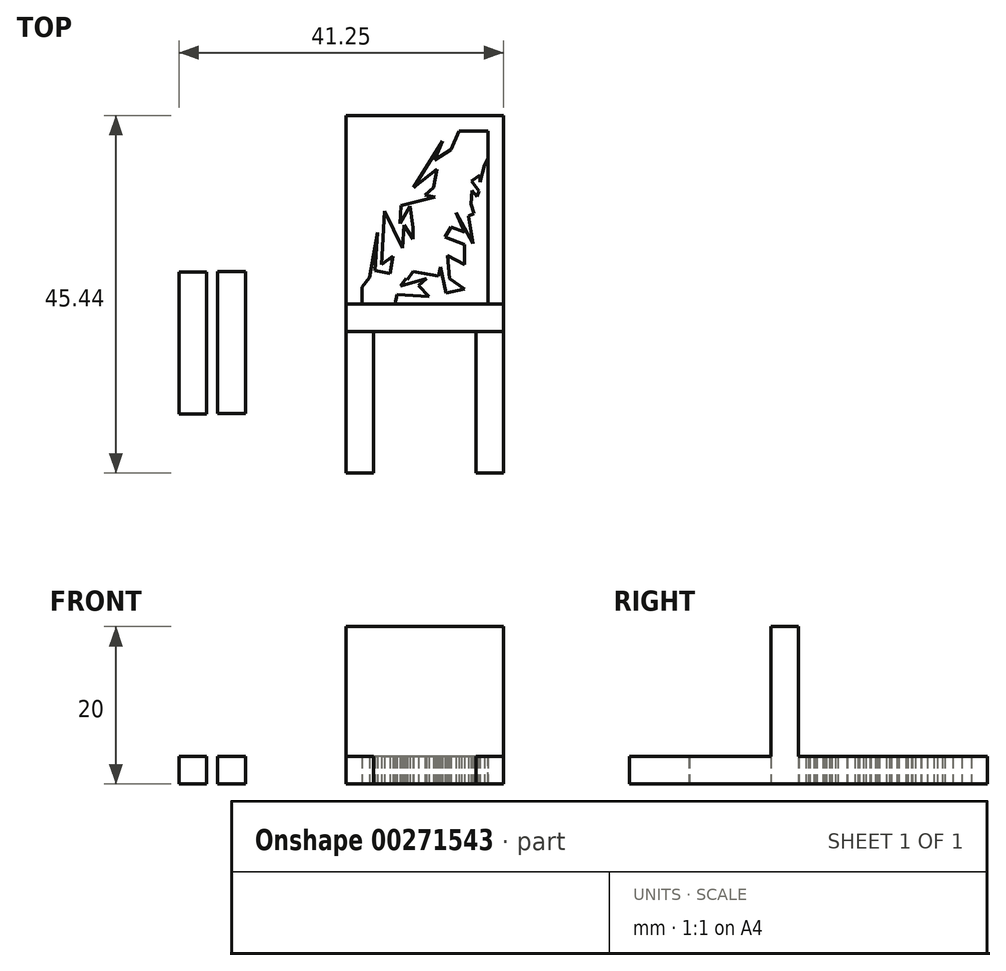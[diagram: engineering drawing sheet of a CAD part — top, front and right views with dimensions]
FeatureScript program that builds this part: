
annotation { "Feature Type Name" : "Feature", "Feature Type Description" : "" }
export const myFeature = defineFeature(function(context is Context, id is Id, definition is map)
    precondition{}
    {
        {
            var Q0;
            Q0=qCreatedBy(makeId("Top.planeOp"),FACE);
            var sketch = newSketch(context, id + "F0", { "sketchPlane" : qUnion([Q0])});
            skLineSegment(sketch, "E0.bottom", {"start": v(10, 1.75) * mm, "end": v(-10, 1.75) * mm});
            skLineSegment(sketch, "E0.top", {"start": v(10, -1.75) * mm, "end": v(-10, -1.75) * mm});
            skLineSegment(sketch, "E0.left", {"start": v(10, 1.75) * mm, "end": v(10, -1.75) * mm});
            skLineSegment(sketch, "E0.right", {"start": v(-10, 1.75) * mm, "end": v(-10, -1.75) * mm});
            skPoint(sketch, "E0.middle", {"position": v(0, 0) * mm});
            skLineSegment(sketch, "E1.bottom", {"start": v(-10, 1.72) * mm, "end": v(10, 1.72) * mm});
            skLineSegment(sketch, "E1.top", {"start": v(-10, 25.72) * mm, "end": v(10, 25.72) * mm});
            skLineSegment(sketch, "E1.left", {"start": v(-10, 1.72) * mm, "end": v(-10, 25.72) * mm});
            skLineSegment(sketch, "E1.right", {"start": v(10, 1.72) * mm, "end": v(10, 25.72) * mm});
            skLineSegment(sketch, "E2.bottom", {"start": v(-10, -1.72) * mm, "end": v(-6.5, -1.72) * mm});
            skLineSegment(sketch, "E2.top", {"start": v(-10, -19.72) * mm, "end": v(-6.5, -19.72) * mm});
            skLineSegment(sketch, "E2.left", {"start": v(-10, -1.72) * mm, "end": v(-10, -19.72) * mm});
            skLineSegment(sketch, "E2.right", {"start": v(-6.5, -1.72) * mm, "end": v(-6.5, -19.72) * mm});
            skLineSegment(sketch, "E3.MirrorCS", {"start": v(6.5, -1.72) * mm, "end": v(6.5, -19.72) * mm});
            skLineSegment(sketch, "E4.MirrorCS", {"start": v(10, -1.72) * mm, "end": v(10, -19.72) * mm});
            skLineSegment(sketch, "E5.MirrorCS", {"start": v(10, -19.72) * mm, "end": v(6.5, -19.72) * mm});
            skLineSegment(sketch, "E6.MirrorCS", {"start": v(10, -1.72) * mm, "end": v(6.5, -1.72) * mm});
            skLineSegment(sketch, "E7.bottom", {"start": v(-8, 1.72) * mm, "end": v(8, 1.72) * mm});
            skLineSegment(sketch, "E7.top", {"start": v(-8, 23.72) * mm, "end": v(8, 23.72) * mm});
            skLineSegment(sketch, "E7.left", {"start": v(-8, 1.72) * mm, "end": v(-8, 23.72) * mm});
            skLineSegment(sketch, "E7.right", {"start": v(8, 1.72) * mm, "end": v(8, 23.72) * mm});
            skSolve(sketch);
        }
        {
            var Q0;
            {var subQ5=sQuery(id+"F0.wireOp",EDGE,"E2.bottom");Q0=makeQuery(id+"F0.imprint","IMPRINT",FACE,{"disambiguationData":[TD([[makeQuery(id+"F0.imprint","IMPRINT",EDGE,{"derivedFrom":subQ5}),1.0]])]});}
            var Q1;
            {var subQ5=sQuery(id+"F0.wireOp",EDGE,"E2.bottom");Q1=makeQuery(id+"F0.imprint","IMPRINT",FACE,{"disambiguationData":[TD([[makeQuery(id+"F0.imprint","IMPRINT",EDGE,{"derivedFrom":subQ5}),-1.0]])]});}
            var Q2;
            {var subQ5=sQuery(id+"F0.wireOp",EDGE,"E6.MirrorCS");Q2=makeQuery(id+"F0.imprint","IMPRINT",FACE,{"disambiguationData":[TD([[makeQuery(id+"F0.imprint","IMPRINT",EDGE,{"derivedFrom":subQ5}),1.0]])]});}
            var Q3;
            {var subQ0=sQuery(id+"F0.wireOp",EDGE,"E7.right");var subQ1=sQuery(id+"F0.wireOp",EDGE,"E0.bottom");var subQ2=makeQuery(id+"F0.imprint","INTERSECT",VERTEX,{"derivedFrom":[subQ1,subQ0]});var subQ5=sQuery(id+"F0.wireOp",EDGE,"E1.bottom");var subQ10=sQuery(id+"F0.wireOp",EDGE,"E0.left");var subQ12=makeQuery(id+"F0.imprint","INTERSECT",VERTEX,{"derivedFrom":[subQ10,subQ5]});var subQ13=sQuery(id+"F0.wireOp",EDGE,"E0.right");var subQ15=makeQuery(id+"F0.imprint","INTERSECT",VERTEX,{"derivedFrom":[subQ13,subQ5]});Q3=qUnion([makeQuery(id+"F0.imprint","IMPRINT",FACE,{"disambiguationData":[TD([[makeQuery(id+"F0.imprint","IMPRINT",EDGE,{"disambiguationData":[TD([[subQ15,-1.0]])],"derivedFrom":subQ5}),1.0]])]}),makeQuery(id+"F0.imprint","IMPRINT",FACE,{"disambiguationData":[TD([[makeQuery(id+"F0.imprint","IMPRINT",EDGE,{"disambiguationData":[TD([[subQ12,1.0]])],"derivedFrom":subQ5}),1.0]])]}),makeQuery(id+"F0.imprint","IMPRINT",FACE,{"disambiguationData":[TD([[makeQuery(id+"F0.imprint","IMPRINT",EDGE,{"disambiguationData":[TD([[subQ2,-1.0]])],"derivedFrom":subQ1}),1.0]])]})]);}
            extrude(context, id + "F1", {"entities" : qUnion([Q0, Q1, Q2, Q3]), "depth" : 20 * mm, "offsetDistance" : 25 * mm});
        }
        {
            var Q0;
            Q0=makeQuery(id+"F0.imprint","IMPRINT",FACE,{"disambiguationData":[TD([[makeQuery(id+"F0.imprint","IMPRINT",EDGE,{"derivedFrom":sQuery(id+"F0.wireOp",EDGE,"E1.top")}),-1.0]])]});
            var Q1;
            {var subQ4=sQuery(id+"F0.wireOp",EDGE,"E2.top");Q1=makeQuery(id+"F0.imprint","IMPRINT",FACE,{"disambiguationData":[TD([[makeQuery(id+"F0.imprint","IMPRINT",EDGE,{"derivedFrom":subQ4}),1.0]])]});}
            var Q2;
            {var subQ3=sQuery(id+"F0.wireOp",EDGE,"E4.MirrorCS");Q2=makeQuery(id+"F0.imprint","IMPRINT",FACE,{"disambiguationData":[TD([[makeQuery(id+"F0.imprint","IMPRINT",EDGE,{"derivedFrom":subQ3}),-1.0]])]});}
            extrude(context, id + "F2", {"entities" : qUnion([Q0, Q1, Q2]), "operationType" : NewBodyOperationType.ADD, "depth" : 3.5 * mm});
        }
        {
            var Q0;
            Q0=qCreatedBy(makeId("Top.planeOp"),FACE);
            var sketch = newSketch(context, id + "F3", { "sketchPlane" : qUnion([Q0])});
            skLineSegment(sketch, "E8.bottom", {"start": v(-31.25, 5.8) * mm, "end": v(-27.75, 5.8) * mm});
            skLineSegment(sketch, "E8.top", {"start": v(-31.25, -12.2) * mm, "end": v(-27.75, -12.2) * mm});
            skLineSegment(sketch, "E8.left", {"start": v(-31.25, 5.8) * mm, "end": v(-31.25, -12.2) * mm});
            skLineSegment(sketch, "E8.right", {"start": v(-27.75, 5.8) * mm, "end": v(-27.75, -12.2) * mm});
            skLineSegment(sketch, "E9.bottom", {"start": v(-26.31, 5.86) * mm, "end": v(-22.81, 5.86) * mm});
            skLineSegment(sketch, "E9.top", {"start": v(-26.31, -12.14) * mm, "end": v(-22.81, -12.14) * mm});
            skLineSegment(sketch, "E9.left", {"start": v(-26.31, 5.86) * mm, "end": v(-26.31, -12.14) * mm});
            skLineSegment(sketch, "E9.right", {"start": v(-22.81, 5.86) * mm, "end": v(-22.81, -12.14) * mm});
            skSolve(sketch);
        }
        {
            var Q0;
            Q0=makeQuery(id+"F3.imprint","IMPRINT",FACE,{"disambiguationData":[TD([[makeQuery(id+"F3.imprint","IMPRINT",EDGE,{"derivedFrom":sQuery(id+"F3.wireOp",EDGE,"E9.bottom")}),-1.0]])]});
            var Q1;
            Q1=makeQuery(id+"F3.imprint","IMPRINT",FACE,{"disambiguationData":[TD([[makeQuery(id+"F3.imprint","IMPRINT",EDGE,{"derivedFrom":sQuery(id+"F3.wireOp",EDGE,"E8.bottom")}),-1.0]])]});
            extrude(context, id + "F4", {"entities" : qUnion([Q0, Q1]), "depth" : 3.5 * mm, "offsetDistance" : 25 * mm});
        }
        {
            var Q0;
            Q0=qCreatedBy(makeId("Top.planeOp"),FACE);
            var sketch = newSketch(context, id + "F5", { "sketchPlane" : qUnion([Q0])});
            skLineSegment(sketch, "E10", {"start": v(-3.81, 1.79) * mm, "end": v(-3.55, 2.97) * mm});
            skLineSegment(sketch, "E11", {"start": v(-3.55, 2.97) * mm, "end": v(0.5, 2.68) * mm});
            skLineSegment(sketch, "E12", {"start": v(0.5, 2.68) * mm, "end": v(-0.78, 4.1) * mm});
            skLineSegment(sketch, "E13", {"start": v(-0.78, 4.1) * mm, "end": v(0.2, 5) * mm});
            skLineSegment(sketch, "E14", {"start": v(0.2, 5) * mm, "end": v(-3.1, 4.04) * mm});
            skLineSegment(sketch, "E15", {"start": v(-3.1, 4.04) * mm, "end": v(-2.43, 4.98) * mm});
            skLineSegment(sketch, "E16", {"start": v(-2.43, 4.98) * mm, "end": v(-2.24, 4.85) * mm});
            skLineSegment(sketch, "E17", {"start": v(-2.24, 4.85) * mm, "end": v(-1.5, 5.9) * mm});
            skLineSegment(sketch, "E18", {"start": v(-1.5, 5.9) * mm, "end": v(1.74, 5.3) * mm});
            skLineSegment(sketch, "E19", {"start": v(1.74, 5.3) * mm, "end": v(1.95, 6.43) * mm});
            skLineSegment(sketch, "E20", {"start": v(1.95, 6.43) * mm, "end": v(2.65, 3.17) * mm});
            skLineSegment(sketch, "E21", {"start": v(2.65, 3.17) * mm, "end": v(5, 3.68) * mm});
            skLineSegment(sketch, "E22", {"start": v(5, 3.68) * mm, "end": v(3.1, 4.98) * mm});
            skLineSegment(sketch, "E23", {"start": v(3.1, 4.98) * mm, "end": v(2.84, 7.92) * mm});
            skLineSegment(sketch, "E24", {"start": v(2.84, 7.92) * mm, "end": v(5.06, 6.76) * mm});
            skLineSegment(sketch, "E25", {"start": v(5.06, 6.76) * mm, "end": v(5.06, 9.3) * mm});
            skLineSegment(sketch, "E26", {"start": v(5.06, 9.3) * mm, "end": v(2.53, 10.29) * mm});
            skLineSegment(sketch, "E27", {"start": v(2.53, 10.29) * mm, "end": v(3.32, 11.54) * mm});
            skLineSegment(sketch, "E28", {"start": v(3.32, 11.54) * mm, "end": v(5.01, 10.93) * mm});
            skLineSegment(sketch, "E29", {"start": v(5.01, 10.93) * mm, "end": v(3.98, 13.37) * mm});
            skLineSegment(sketch, "E30", {"start": v(3.98, 13.37) * mm, "end": v(6.1, 9.45) * mm});
            skLineSegment(sketch, "E31", {"start": v(6.1, 9.45) * mm, "end": v(5.55, 12.93) * mm});
            skLineSegment(sketch, "E32", {"start": v(5.55, 12.93) * mm, "end": v(6.21, 13.27) * mm});
            skLineSegment(sketch, "E33", {"start": v(6.21, 13.27) * mm, "end": v(5.86, 14.47) * mm});
            skLineSegment(sketch, "E34", {"start": v(5.86, 14.47) * mm, "end": v(6.01, 16.2) * mm});
            skLineSegment(sketch, "E35", {"start": v(6.01, 16.2) * mm, "end": v(6.6, 15.39) * mm});
            skLineSegment(sketch, "E36", {"start": v(6.6, 15.39) * mm, "end": v(6.87, 16.1) * mm});
            skLineSegment(sketch, "E37", {"start": v(6.87, 16.1) * mm, "end": v(5.95, 17.35) * mm});
            skLineSegment(sketch, "E38", {"start": v(5.95, 17.35) * mm, "end": v(7, 18.12) * mm});
            skLineSegment(sketch, "E39", {"start": v(7, 18.12) * mm, "end": v(7, 17.28) * mm});
            skLineSegment(sketch, "E40", {"start": v(7, 17.28) * mm, "end": v(7.59, 19.4) * mm});
            skLineSegment(sketch, "E41", {"start": v(7.59, 19.4) * mm, "end": v(8, 20.3) * mm});
            skLineSegment(sketch, "E42", {"start": v(8, 20.3) * mm, "end": v(8, 1.73) * mm});
            skLineSegment(sketch, "E43", {"start": v(8, 1.73) * mm, "end": v(-3.81, 1.79) * mm});
            skLineSegment(sketch, "E44", {"start": v(-8, 8.56) * mm, "end": v(-8, 23.72) * mm});
            skLineSegment(sketch, "E45", {"start": v(-8, 23.72) * mm, "end": v(4.35, 23.72) * mm});
            skLineSegment(sketch, "E46", {"start": v(4.35, 23.72) * mm, "end": v(3.34, 21.37) * mm});
            skLineSegment(sketch, "E47", {"start": v(3.34, 21.37) * mm, "end": v(1.21, 20.02) * mm});
            skLineSegment(sketch, "E48", {"start": v(1.21, 20.02) * mm, "end": v(2.26, 22.49) * mm});
            skLineSegment(sketch, "E49", {"start": v(2.26, 22.49) * mm, "end": v(-1.44, 16.58) * mm});
            skLineSegment(sketch, "E50", {"start": v(-3.27, 11.83) * mm, "end": v(-1.9, 14.23) * mm});
            skLineSegment(sketch, "E51", {"start": v(-1.9, 14.23) * mm, "end": v(-1.52, 11.5) * mm});
            skLineSegment(sketch, "E52", {"start": v(-2.86, 8.88) * mm, "end": v(-5.14, 13.55) * mm});
            skLineSegment(sketch, "E53", {"start": v(-5.14, 13.55) * mm, "end": v(-5.48, 6.75) * mm});
            skLineSegment(sketch, "E54", {"start": v(-5.48, 6.75) * mm, "end": v(-4.02, 7.87) * mm});
            skLineSegment(sketch, "E55", {"start": v(-4.02, 7.87) * mm, "end": v(-4.43, 5.66) * mm});
            skLineSegment(sketch, "E56", {"start": v(-4.43, 5.66) * mm, "end": v(-6.32, 6) * mm});
            skLineSegment(sketch, "E57", {"start": v(-6.32, 6) * mm, "end": v(-6, 10.82) * mm});
            skLineSegment(sketch, "E58", {"start": v(-6, 10.82) * mm, "end": v(-7.05, 5.1) * mm});
            skLineSegment(sketch, "E59", {"start": v(-7.05, 5.1) * mm, "end": v(-8, 3.9) * mm});
            skLineSegment(sketch, "E60", {"start": v(-8, 3.9) * mm, "end": v(-8, 8.56) * mm});
            skLineSegment(sketch, "E61", {"start": v(-1.44, 16.58) * mm, "end": v(1.55, 18.94) * mm});
            skLineSegment(sketch, "E62", {"start": v(1.55, 18.94) * mm, "end": v(1.12, 16.58) * mm});
            skLineSegment(sketch, "E63", {"start": v(1.12, 16.58) * mm, "end": v(0, 15.6) * mm});
            skLineSegment(sketch, "E64", {"start": v(0, 15.6) * mm, "end": v(1.29, 15.37) * mm});
            skLineSegment(sketch, "E65", {"start": v(1.29, 15.37) * mm, "end": v(-3.05, 14.26) * mm});
            skLineSegment(sketch, "E66", {"start": v(-3.05, 14.26) * mm, "end": v(-3.17, 12) * mm});
            skLineSegment(sketch, "E67", {"start": v(-2.86, 8.88) * mm, "end": v(-2.66, 11.8) * mm});
            skLineSegment(sketch, "E68", {"start": v(-2.66, 11.8) * mm, "end": v(-1.52, 10) * mm});
            skLineSegment(sketch, "E69", {"start": v(-1.52, 10) * mm, "end": v(-1.52, 11.5) * mm});
            skSolve(sketch);
        }
        {
            var Q0;
            Q0=makeQuery(id+"F5.imprint","IMPRINT",FACE,{"disambiguationData":[TD([[makeQuery(id+"F5.imprint","IMPRINT",EDGE,{"derivedFrom":sQuery(id+"F5.wireOp",EDGE,"E44")}),-1.0]])]});
            var Q1;
            Q1=makeQuery(id+"F5.imprint","IMPRINT",FACE,{"disambiguationData":[TD([[makeQuery(id+"F5.imprint","IMPRINT",EDGE,{"derivedFrom":sQuery(id+"F5.wireOp",EDGE,"E10")}),-1.0]])]});
            extrude(context, id + "F6", {"entities" : qUnion([Q0, Q1]), "operationType" : NewBodyOperationType.ADD, "depth" : 3.5 * mm, "offsetDistance" : 25 * mm});
        }
    });
